# Revit family: QF_GIORIK_SERE061W
name_source: partatom
category: Specialty Equipment
revit_build: Autodesk Revit 2016 (Build: 20150220_1215(x64)
units: mm (PartAtom-declared; Revit-internal decimal feet)

## family parameters
Always vertical = Yes
Cut with Voids When Loaded = No
OmniClass Number = 23.21.21.13.31.13
Part Type = Normal
Room Calculation Point = No
Round Connector Dimension = Use Diameter
Shared = No
Work Plane-Based = No

## types (1)
- SERE061W
    Apparent Power = 11400 VA
    Assembly Code = E1090320
    Cold Water Connection Height = 115 mm  [stored 0.377297 ft]
    Cold Water Size = 1"
    Cold Water Temperature Recommended = 0 °C
    Cycle = 50 Hz
    Description = ELECTRIC OVEN 6 GN 1/1 COMBINED CONVECTION/STEAM WITH DIRECT INJECTION AND WASHING SYSTEM
    FL Amps = 0 A
    HP = 0
    Indirect Waste Connection Height = 77 mm  [stored 0.252625 ft]
    Indirect Waste Flow = 0.0 L/s
    Indirect Waste Size = 2"
    Manufacturer = GIORIK
    Max Overcurrent Protection = 20 A
    Min Ckt Ampacity = 0 A
    Model = SERE061W
    Phase = 3
    Touch screen control = Yes
    URL = www.welbilt.com
    Volts = 400 V
    Waste Water Discharge Temperature = 0 °C
    Watts = 11400 W
    Weight in Pounds = 291.01

note: [stored X ft] marks values corroborated as IEEE doubles in the binary element streams (Revit-internal decimal feet)

## geometry (parser evidence)
native form markers: Blend x5, Sweep x1
no freeform markers — native parametric forms only
